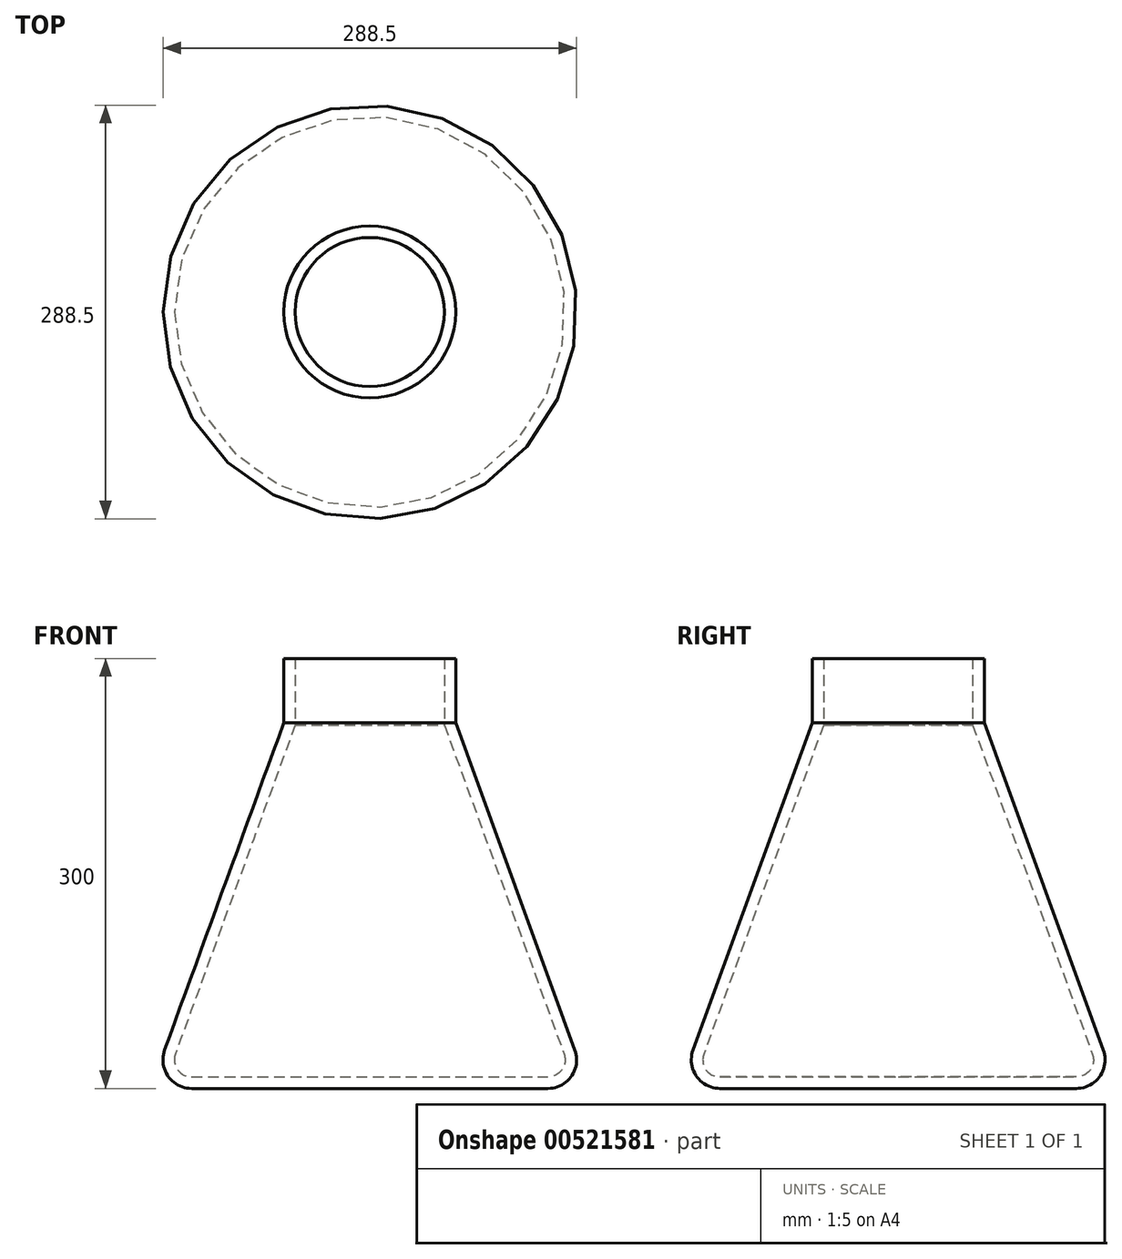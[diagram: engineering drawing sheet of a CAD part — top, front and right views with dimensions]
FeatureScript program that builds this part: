
annotation { "Feature Type Name" : "Feature", "Feature Type Description" : "" }
export const myFeature = defineFeature(function(context is Context, id is Id, definition is map)
    precondition{}
    {
        {
            var Q0;
            Q0=qCreatedBy(makeId("Front.planeOp"),FACE);
            var sketch = newSketch(context, id + "F0", { "sketchPlane" : qUnion([Q0])});
            skLineSegment(sketch, "E0", {"start": v(0, 0) * mm, "end": v(124.25, 0) * mm});
            skLineSegment(sketch, "E1", {"start": v(143.04, 26.84) * mm, "end": v(60, 255) * mm});
            skLineSegment(sketch, "E2", {"start": v(60, 255) * mm, "end": v(60, 300) * mm});
            skLineSegment(sketch, "E3", {"start": v(0, 0) * mm, "end": v(0, 8) * mm});
            skPoint(sketch, "E4.visualSharp", {"position": v(152.81, 0) * mm});
            skArc(sketch, "E4.filletArc", {"start": v(124.25, 0) * mm, "mid": v(140.63, 8.53) * mm, "end": v(143.04, 26.84) * mm});
            skLineSegment(sketch, "E5.0", {"start": v(52, 253.59) * mm, "end": v(52, 300) * mm});
            skLineSegment(sketch, "E5.1", {"start": v(135.53, 24.1) * mm, "end": v(52, 253.59) * mm});
            skArc(sketch, "E5.2", {"start": v(124.25, 8) * mm, "mid": v(134.08, 13.12) * mm, "end": v(135.53, 24.1) * mm});
            skLineSegment(sketch, "E5.3", {"start": v(0, 8) * mm, "end": v(124.25, 8) * mm});
            skLineSegment(sketch, "E6", {"start": v(52, 300) * mm, "end": v(60, 300) * mm});
            skSolve(sketch);
        }
        {
            var Q0;
            Q0 = qSketchRegion(id + "F0", true);
            var Q1;
            Q1=sQuery(id+"F0.wireOp",EDGE,"E3");
            revolve(context, id + "F1", {"entities" : qUnion([Q0]), "axis" : qUnion([Q1]), "revolveType" : RevolveType.FULL});
        }
    });
